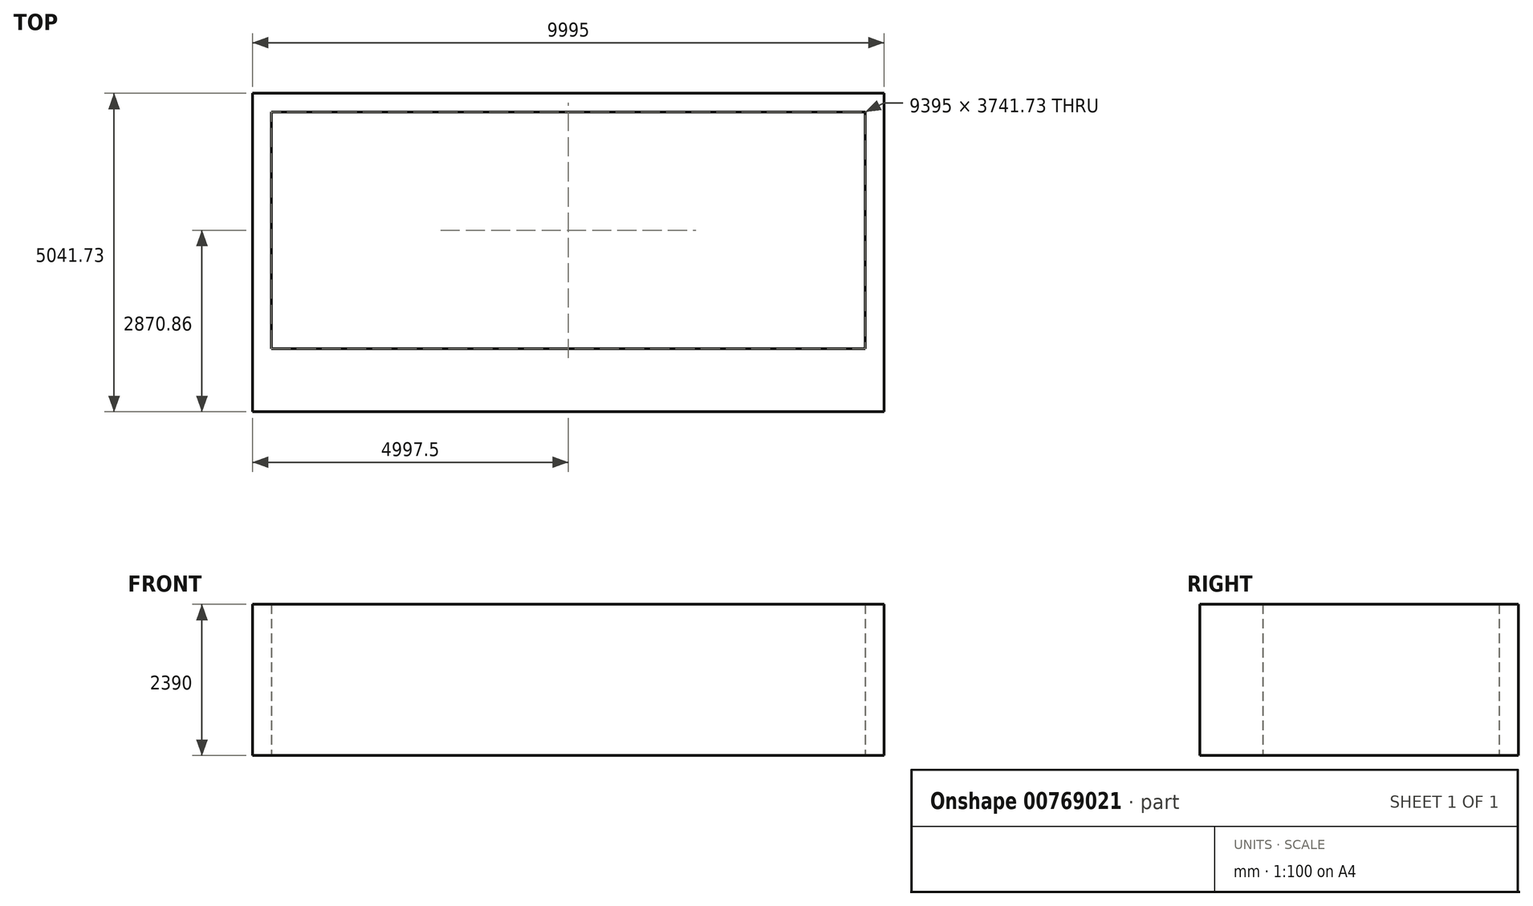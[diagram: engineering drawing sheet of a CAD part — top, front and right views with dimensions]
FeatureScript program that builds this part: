
annotation { "Feature Type Name" : "Feature", "Feature Type Description" : "" }
export const myFeature = defineFeature(function(context is Context, id is Id, definition is map)
    precondition{}
    {
        {
            var Q0;
            Q0=qCreatedBy(makeId("Top.planeOp"),FACE);
            var sketch = newSketch(context, id + "F0", { "sketchPlane" : qUnion([Q0])});
            skLineSegment(sketch, "E0.bottom", {"start": v(-5002.45, 2524.06) * mm, "end": v(4997.55, 2524.06) * mm});
            skLineSegment(sketch, "E0.top", {"start": v(-5002.45, -2522.67) * mm, "end": v(4997.55, -2522.67) * mm});
            skLineSegment(sketch, "E0.left", {"start": v(-5002.45, 2524.06) * mm, "end": v(-5002.45, -2522.67) * mm});
            skLineSegment(sketch, "E0.right", {"start": v(4997.55, 2524.06) * mm, "end": v(4997.55, -2522.67) * mm});
            skLineSegment(sketch, "E1.0", {"start": v(-4997.45, 2519.06) * mm, "end": v(4997.55, 2519.06) * mm});
            skLineSegment(sketch, "E1.1", {"start": v(-4997.45, 2519.06) * mm, "end": v(-4997.45, -2522.67) * mm});
            skLineSegment(sketch, "E2.0", {"start": v(-4697.45, 2219.06) * mm, "end": v(4697.55, 2219.06) * mm});
            skLineSegment(sketch, "E3.0", {"start": v(-4697.45, 2219.06) * mm, "end": v(-4697.45, -1522.67) * mm});
            skLineSegment(sketch, "E4.0", {"start": v(-5002.45, -1522.67) * mm, "end": v(-4997.45, -1522.67) * mm});
            skLineSegment(sketch, "E5.0", {"start": v(4697.55, 2524.06) * mm, "end": v(4697.55, 2519.06) * mm});
            skLineSegment(sketch, "E6.trimOffspring", {"start": v(-4697.45, -1522.67) * mm, "end": v(4697.55, -1522.67) * mm});
            skLineSegment(sketch, "E7.trimOffspring", {"start": v(4697.55, 2219.06) * mm, "end": v(4697.55, -1522.67) * mm});
            skSolve(sketch);
        }
        {
            var Q0;
            Q0=makeQuery(id+"F0.imprint","IMPRINT",FACE,{"disambiguationData":[TD([[makeQuery(id+"F0.imprint","IMPRINT",EDGE,{"derivedFrom":sQuery(id+"F0.wireOp",EDGE,"E2.0")}),1.0]])]});
            extrude(context, id + "F1", {"entities" : qUnion([Q0]), "depth" : 2390 * mm, "offsetDistance" : 25 * mm});
        }
        {
            var Q0;
            Q0=makeQuery(id+"F1.opExtrude","SWEPT_FACE",FACE,{"disambiguationData":[OSD([sQuery(id+"F0.wireOp",EDGE,"E0.top")])]});
            var sketch = newSketch(context, id + "F2", { "sketchPlane" : qUnion([Q0])});
            skLineSegment(sketch, "E8.bottom", {"start": v(-1645.6, 1782.84) * mm, "end": v(1717, 1782.84) * mm});
            skLineSegment(sketch, "E8.top", {"start": v(-1645.6, 644.5) * mm, "end": v(1717, 644.5) * mm});
            skLineSegment(sketch, "E8.left", {"start": v(-1645.6, 1782.84) * mm, "end": v(-1645.6, 644.5) * mm});
            skLineSegment(sketch, "E8.right", {"start": v(1717, 1782.84) * mm, "end": v(1717, 644.5) * mm});
            skSolve(sketch);
        }
        {
            var Q0;
            Q0=makeQuery(id+"F2.imprint","IMPRINT",FACE,{"disambiguationData":[TD([[makeQuery(id+"F2.imprint","IMPRINT",EDGE,{"derivedFrom":sQuery(id+"F2.wireOp",EDGE,"E8.bottom")}),-1.0]])]});
            extrude(context, id + "F3", {"entities" : qUnion([Q0]), "operationType" : NewBodyOperationType.ADD, "oppositeDirection" : true, "depth" : 990 * mm, "offsetDistance" : 25 * mm});
        }
    });
